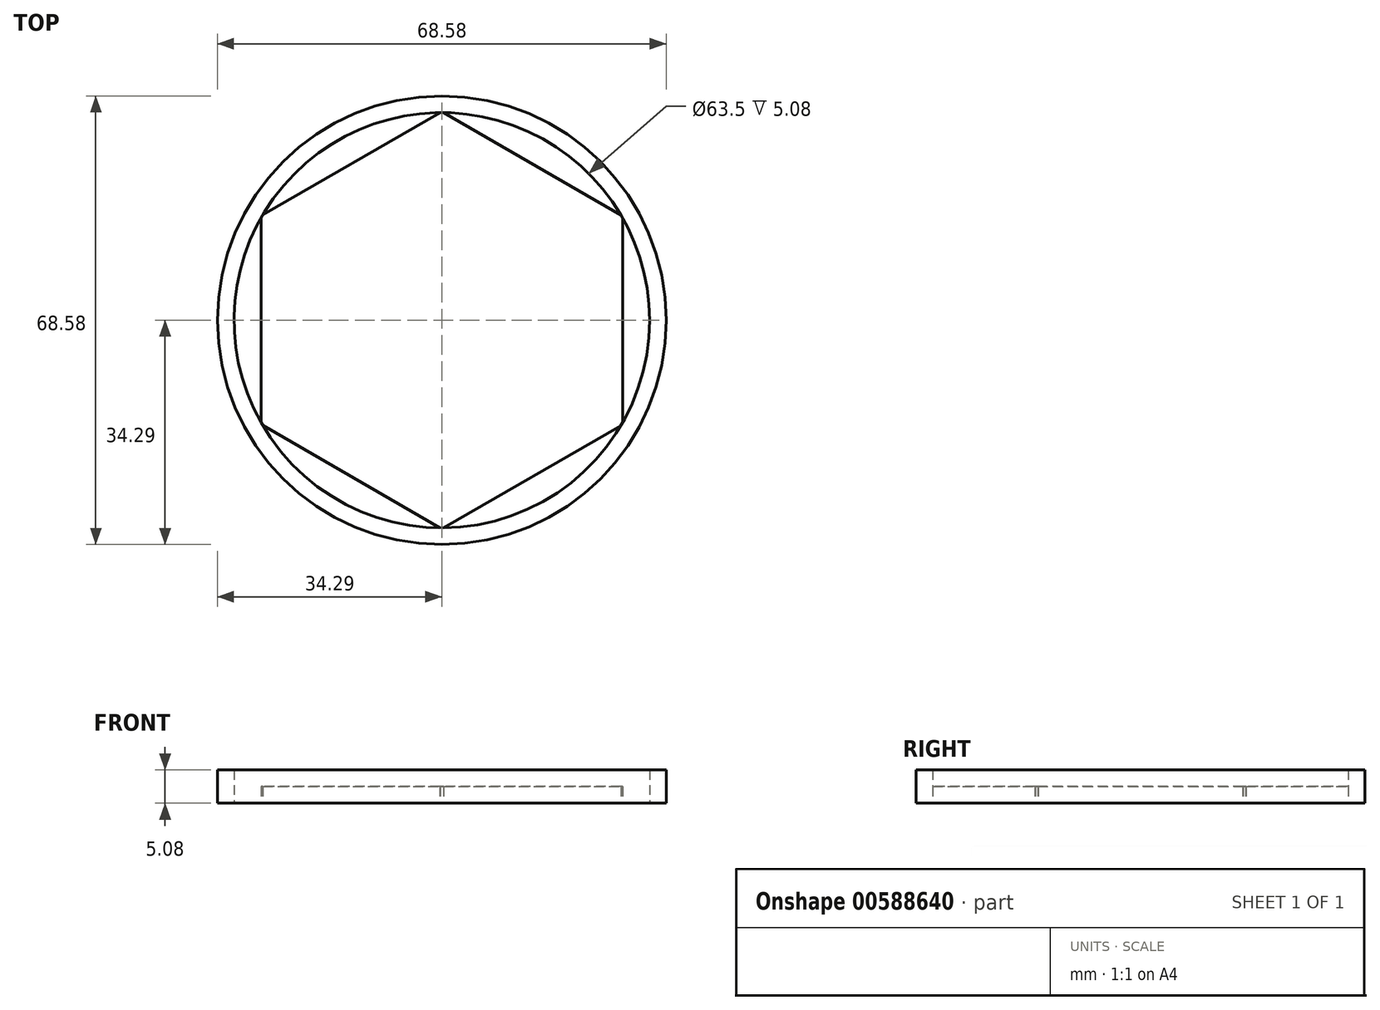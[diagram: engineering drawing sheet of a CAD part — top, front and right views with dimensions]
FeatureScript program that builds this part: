
annotation { "Feature Type Name" : "Feature", "Feature Type Description" : "" }
export const myFeature = defineFeature(function(context is Context, id is Id, definition is map)
    precondition{}
    {
        {
            var Q0;
            Q0=qCreatedBy(makeId("Top.planeOp"),FACE);
            var sketch = newSketch(context, id + "F0", { "sketchPlane" : qUnion([Q0])});
            skCircle(sketch, "E0", {"center": v(0, 0) * mm, "radius": 31.75 * mm});
            skCircle(sketch, "E1", {"center": v(0, 0) * mm, "radius": 34.3 * mm});
            skSolve(sketch);
        }
        {
            var Q0;
            Q0=makeQuery(id+"F0.imprint","IMPRINT",FACE,{"disambiguationData":[TD([[makeQuery(id+"F0.imprint","IMPRINT",EDGE,{"derivedFrom":sQuery(id+"F0.wireOp",EDGE,"E0")}),-1.0]])]});
            extrude(context, id + "F1", {"entities" : qUnion([Q0]), "depth" : 5.08 * mm, "offsetDistance" : 25.4 * mm});
        }
        {
            var Q0;
            Q0=qCreatedBy(makeId("Top.planeOp"),FACE);
            var sketch = newSketch(context, id + "F2", { "sketchPlane" : qUnion([Q0])});
            skCircle(sketch, "E2.cCircle", {"center": v(0, 0) * mm, "radius": 27.63 * mm, "construction": true});
            skLineSegment(sketch, "E2.0", {"start": v(0.01, 31.9) * mm, "end": v(27.63, 15.94) * mm});
            skLineSegment(sketch, "E2.1", {"start": v(27.63, 15.94) * mm, "end": v(27.62, -15.96) * mm});
            skLineSegment(sketch, "E2.2", {"start": v(27.62, -15.96) * mm, "end": v(-0.01, -31.9) * mm});
            skLineSegment(sketch, "E2.3", {"start": v(-0.01, -31.9) * mm, "end": v(-27.63, -15.94) * mm});
            skLineSegment(sketch, "E2.4", {"start": v(-27.63, -15.94) * mm, "end": v(-27.62, 15.96) * mm});
            skLineSegment(sketch, "E2.5", {"start": v(-27.62, 15.96) * mm, "end": v(0.01, 31.9) * mm});
            skPoint(sketch, "E2.0.midPoint", {"position": v(13.82, 23.92) * mm});
            skSolve(sketch);
        }
        {
            var Q0;
            Q0=makeQuery(id+"F2.imprint","IMPRINT",FACE,{"disambiguationData":[TD([[makeQuery(id+"F2.imprint","IMPRINT",EDGE,{"derivedFrom":sQuery(id+"F2.wireOp",EDGE,"E2.0")}),-1.0]])]});
            extrude(context, id + "F3", {"entities" : qUnion([Q0]), "operationType" : NewBodyOperationType.ADD, "depth" : 2.54 * mm, "offsetDistance" : 25.4 * mm});
        }
    });
